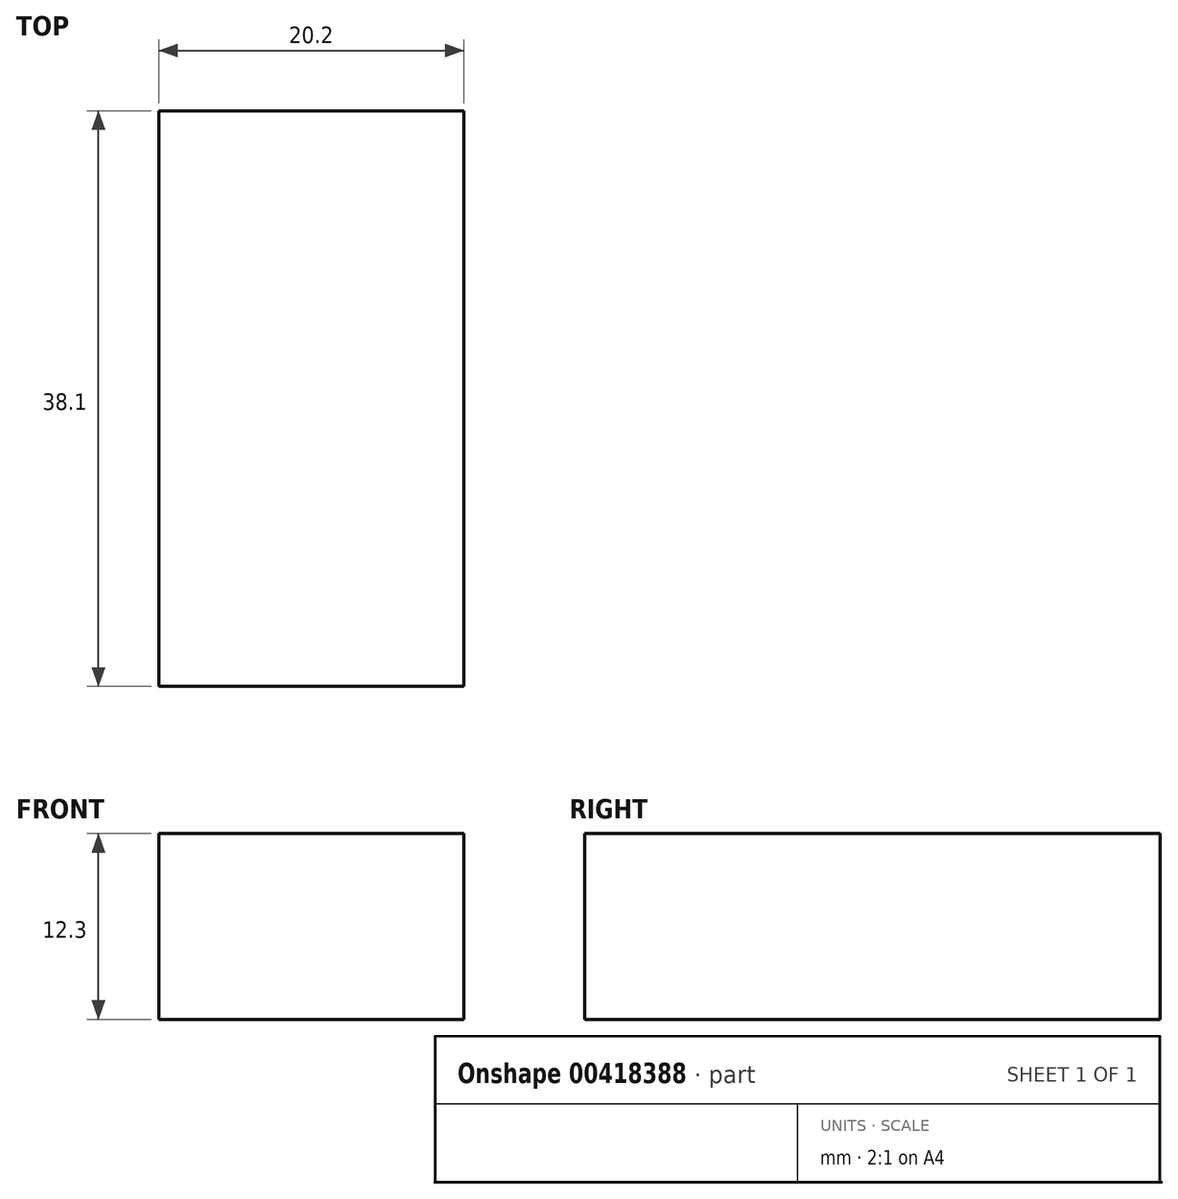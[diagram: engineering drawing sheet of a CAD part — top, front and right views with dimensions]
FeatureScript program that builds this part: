
annotation { "Feature Type Name" : "Feature", "Feature Type Description" : "" }
export const myFeature = defineFeature(function(context is Context, id is Id, definition is map)
    precondition{}
    {
        {
            var Q0;
            Q0=qCreatedBy(makeId("Top.planeOp"),FACE);
            var sketch = newSketch(context, id + "F0", { "sketchPlane" : qUnion([Q0])});
            skLineSegment(sketch, "E0.bottom", {"start": v(10.1, 19.05) * mm, "end": v(-10.1, 19.05) * mm});
            skLineSegment(sketch, "E0.top", {"start": v(10.1, -19.05) * mm, "end": v(-10.1, -19.05) * mm});
            skLineSegment(sketch, "E0.left", {"start": v(10.1, 19.05) * mm, "end": v(10.1, -19.05) * mm});
            skLineSegment(sketch, "E0.right", {"start": v(-10.1, 19.05) * mm, "end": v(-10.1, -19.05) * mm});
            skPoint(sketch, "E0.middle", {"position": v(0, 0) * mm});
            skSolve(sketch);
        }
        {
            var Q0;
            Q0 = qSketchRegion(id + "F0", true);
            extrude(context, id + "F1", {"entities" : qUnion([Q0]), "depth" : 12.3 * mm});
        }
    });
